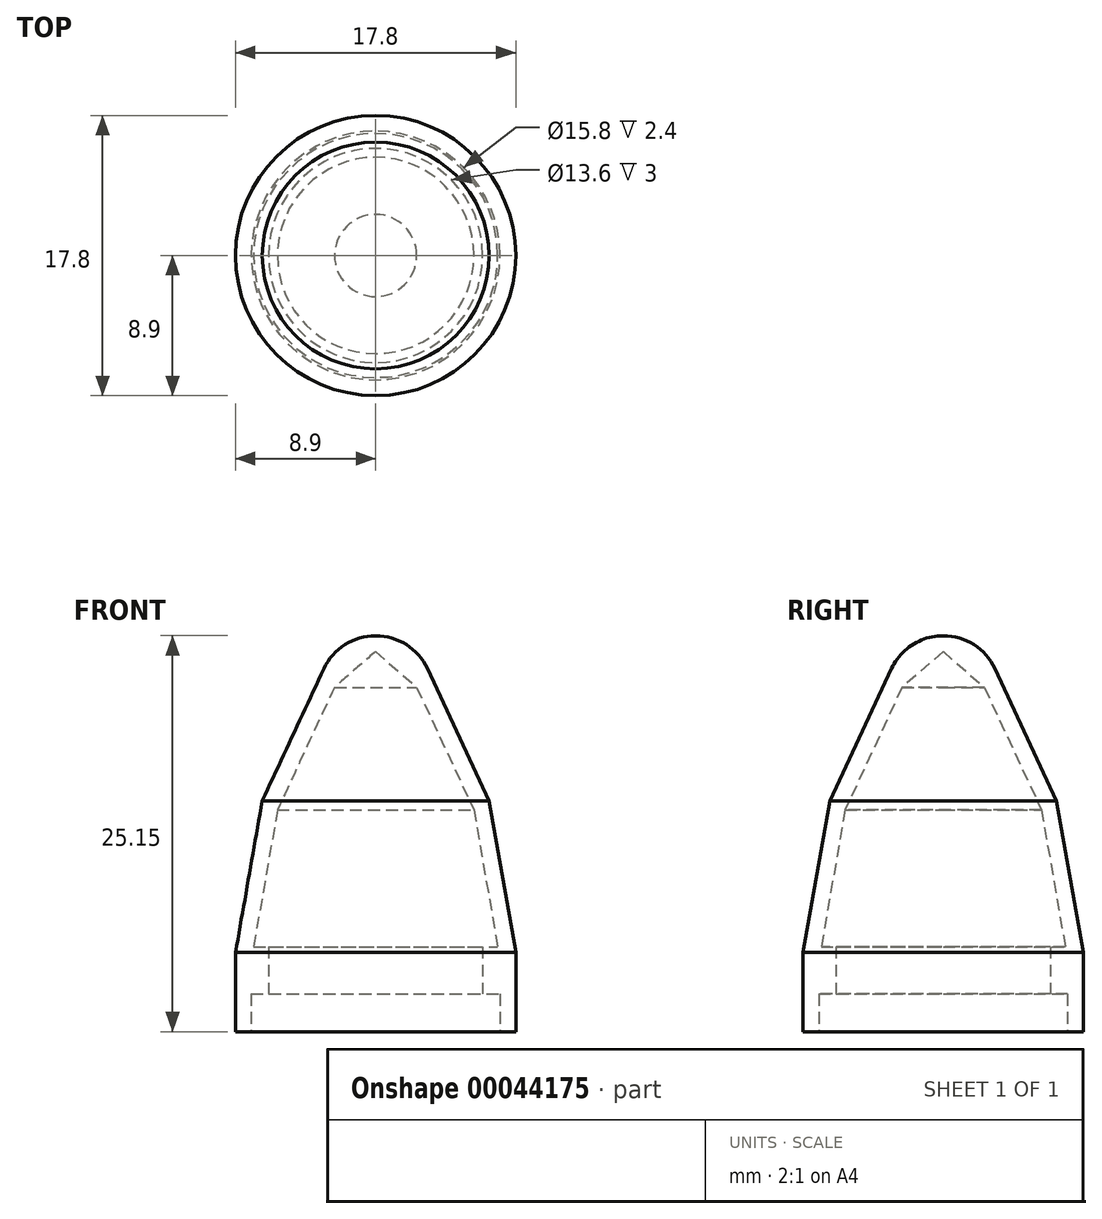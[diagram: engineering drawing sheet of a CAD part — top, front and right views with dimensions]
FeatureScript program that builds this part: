
annotation { "Feature Type Name" : "Feature", "Feature Type Description" : "" }
export const myFeature = defineFeature(function(context is Context, id is Id, definition is map)
    precondition{}
    {
        {
            var Q0;
            Q0=qCreatedBy(makeId("Top.planeOp"),FACE);
            var sketch = newSketch(context, id + "F0", { "sketchPlane" : qUnion([Q0])});
            skLineSegment(sketch, "E0", {"start": v(-17.52, 0) * mm, "end": v(42.68, 0) * mm, "construction": true});
            skLineSegment(sketch, "E1", {"start": v(0, 0) * mm, "end": v(0, 7.9) * mm, "construction": true});
            skLineSegment(sketch, "E2", {"start": v(0, 7.9) * mm, "end": v(2.4, 7.9) * mm});
            skLineSegment(sketch, "E3", {"start": v(2.4, 6.8) * mm, "end": v(2.4, 7.9) * mm});
            skLineSegment(sketch, "E4", {"start": v(2.4, 6.8) * mm, "end": v(5.4, 6.8) * mm});
            skLineSegment(sketch, "E5", {"start": v(0, 7.9) * mm, "end": v(0, 8.9) * mm});
            skLineSegment(sketch, "E6", {"start": v(5.4, 6.8) * mm, "end": v(5.4, 7.75) * mm});
            skLineSegment(sketch, "E7", {"start": v(0, 8.9) * mm, "end": v(5.03, 8.9) * mm});
            skLineSegment(sketch, "E8", {"start": v(5.03, 8.9) * mm, "end": v(14.66, 7.2) * mm});
            skLineSegment(sketch, "E9", {"start": v(14.66, 7.2) * mm, "end": v(23.06, 3.29) * mm});
            skLineSegment(sketch, "E10", {"start": v(5.4, 7.75) * mm, "end": v(14.1, 6.24) * mm});
            skLineSegment(sketch, "E11", {"start": v(14.1, 6.24) * mm, "end": v(21.87, 2.6) * mm});
            skLineSegment(sketch, "E12", {"start": v(21.87, 2.6) * mm, "end": v(24.15, 0) * mm});
            skLineSegment(sketch, "E13", {"start": v(24.15, 0) * mm, "end": v(25.15, 0) * mm});
            skArc(sketch, "E14", {"start": v(23.06, 3.29) * mm, "mid": v(24.58, 1.95) * mm, "end": v(25.15, 0) * mm});
            skSolve(sketch);
        }
        {
            var Q0;
            Q0=makeQuery(id+"F0.imprint","IMPRINT",FACE,{"disambiguationData":[TD([[makeQuery(id+"F0.imprint","IMPRINT",EDGE,{"derivedFrom":sQuery(id+"F0.wireOp",EDGE,"E2")}),1.0]])]});
            var Q1;
            Q1=sQuery(id+"F0.wireOp",EDGE,"E0");
            revolve(context, id + "F1", {"entities" : qUnion([Q0]), "axis" : qUnion([Q1]), "revolveType" : RevolveType.FULL});
        }
        {
            var Q0;
            Q0=qCreatedBy(makeId("Front.planeOp"),FACE);
            var sketch = newSketch(context, id + "F2", { "sketchPlane" : qUnion([Q0])});
            skCircle(sketch, "E15", {"center": v(0, 0) * mm, "radius": 7.65 * mm});
            skSolve(sketch);
        }
        {
            var Q0;
            Q0=makeQuery(id+"F1.opRevolve","SWEPT_BODY",BODY,{"disambiguationData":[OSD([sQuery(id+"F0.wireOp",EDGE,"E2"),sQuery(id+"F0.wireOp",EDGE,"E3"),sQuery(id+"F0.wireOp",EDGE,"E4"),sQuery(id+"F0.wireOp",EDGE,"E5"),sQuery(id+"F0.wireOp",EDGE,"E6"),sQuery(id+"F0.wireOp",EDGE,"E7"),sQuery(id+"F0.wireOp",EDGE,"E8"),sQuery(id+"F0.wireOp",EDGE,"E9"),sQuery(id+"F0.wireOp",EDGE,"E10"),sQuery(id+"F0.wireOp",EDGE,"E11"),sQuery(id+"F0.wireOp",EDGE,"E12"),sQuery(id+"F0.wireOp",EDGE,"E13"),sQuery(id+"F0.wireOp",EDGE,"E14")])]});
            var Q1;
            Q1=sQuery(id+"F2.wireOp",EDGE,"E15");
            transform(context, id + "F3", {"entities" : qUnion([Q0]), "transformType" : TransformType.ROTATION, "transformAxis" : qUnion([Q1]), "angle" : 90 * degree, "makeCopy" : false});
        }
    });
